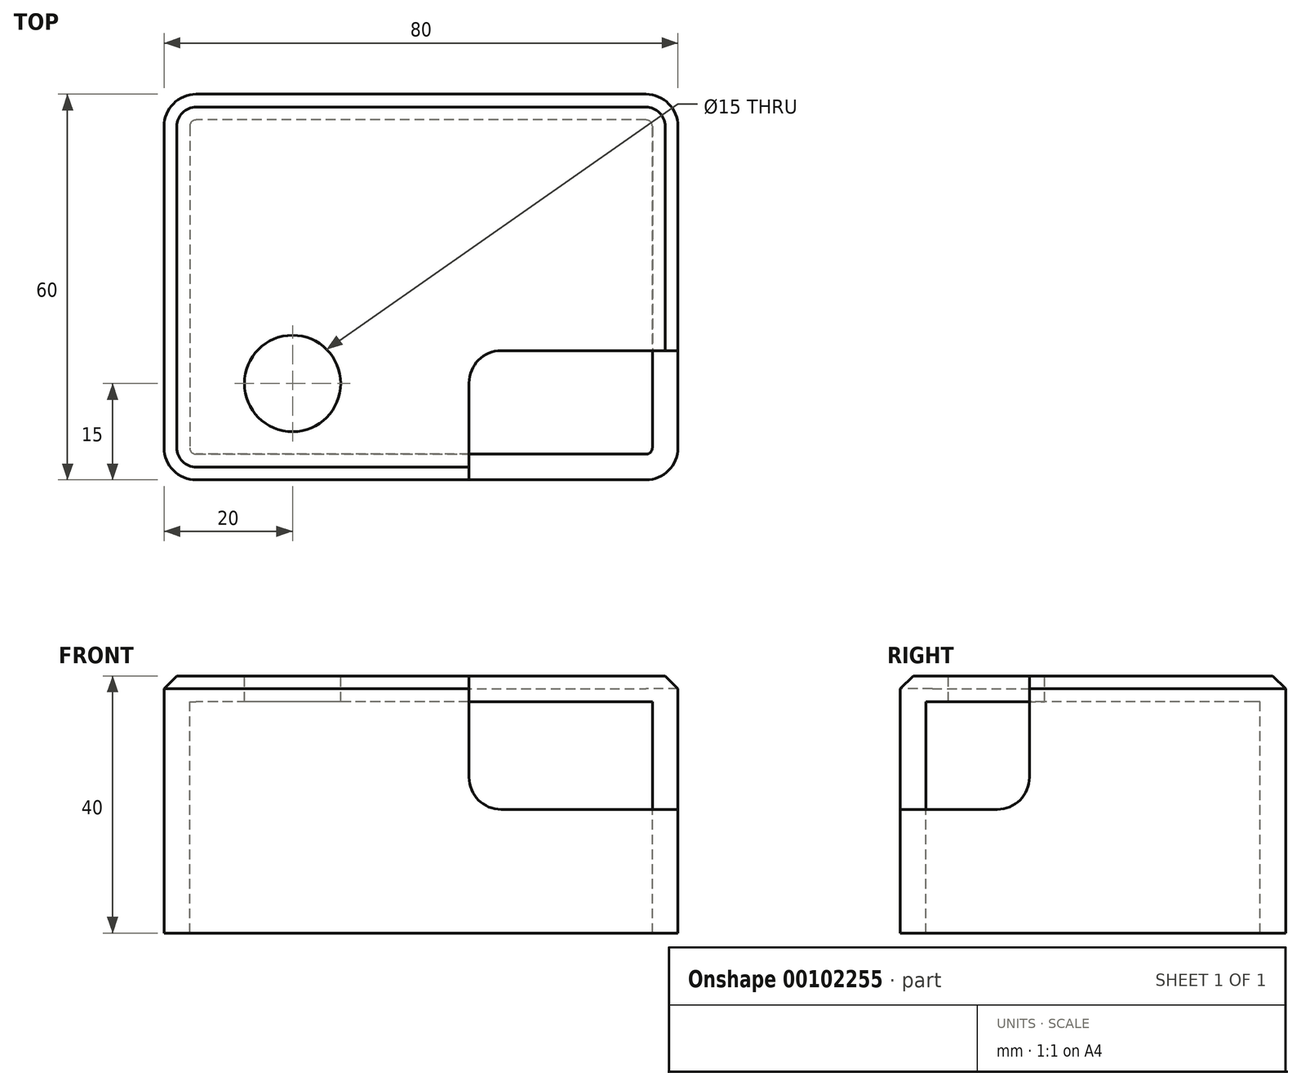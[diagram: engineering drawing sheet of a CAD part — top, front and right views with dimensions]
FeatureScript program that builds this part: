
annotation { "Feature Type Name" : "Feature", "Feature Type Description" : "" }
export const myFeature = defineFeature(function(context is Context, id is Id, definition is map)
    precondition{}
    {
        {
            var Q0;
            Q0=qCreatedBy(makeId("Top.planeOp"),FACE);
            var sketch = newSketch(context, id + "F0", { "sketchPlane" : qUnion([Q0])});
            skLineSegment(sketch, "E0.bottom", {"start": v(0, 0) * mm, "end": v(80, 0) * mm});
            skLineSegment(sketch, "E0.top", {"start": v(0, 60) * mm, "end": v(80, 60) * mm});
            skLineSegment(sketch, "E0.left", {"start": v(0, 0) * mm, "end": v(0, 60) * mm});
            skLineSegment(sketch, "E0.right", {"start": v(80, 0) * mm, "end": v(80, 60) * mm});
            skSolve(sketch);
        }
        {
            var Q0;
            Q0=makeQuery(id+"F0.imprint","IMPRINT",FACE,{"disambiguationData":[TD([[makeQuery(id+"F0.imprint","IMPRINT",EDGE,{"derivedFrom":sQuery(id+"F0.wireOp",EDGE,"E0.bottom")}),1.0]])]});
            extrude(context, id + "F1", {"entities" : qUnion([Q0]), "depth" : 40 * mm});
        }
        {
            var Q0;
            Q0=makeQuery(id+"F1.opExtrude","SWEPT_EDGE",EDGE,{"disambiguationData":[OSD([sQuery(id+"F0.wireOp",EDGE,"E0.top"),sQuery(id+"F0.wireOp",EDGE,"E0.right")])]});
            var Q1;
            Q1=makeQuery(id+"F1.opExtrude","SWEPT_EDGE",EDGE,{"disambiguationData":[OSD([sQuery(id+"F0.wireOp",EDGE,"E0.bottom"),sQuery(id+"F0.wireOp",EDGE,"E0.right")])]});
            var Q2;
            Q2=makeQuery(id+"F1.opExtrude","SWEPT_EDGE",EDGE,{"disambiguationData":[OSD([sQuery(id+"F0.wireOp",EDGE,"E0.bottom"),sQuery(id+"F0.wireOp",EDGE,"E0.left")])]});
            var Q3;
            Q3=makeQuery(id+"F1.opExtrude","SWEPT_EDGE",EDGE,{"disambiguationData":[OSD([sQuery(id+"F0.wireOp",EDGE,"E0.top"),sQuery(id+"F0.wireOp",EDGE,"E0.left")])]});
            fillet(context, id + "F2", {"entities" : qUnion([Q0, Q1, Q2, Q3]), "radius" : 5 * mm, "tangentPropagation" : true, "allowEdgeOverflow" : false});
        }
        {
            var Q0;
            Q0=makeQuery(id+"F1.opExtrude","CAP_EDGE",EDGE,{"disambiguationData":[OSD([sQuery(id+"F0.wireOp",EDGE,"E0.bottom")])],"isStart":false});
            chamfer(context, id + "F3", {"entities" : qUnion([Q0]), "width" : 2 * mm, "tangentPropagation" : true});
        }
        {
            var Q0;
            Q0=makeQuery(id+"F1.opExtrude","CAP_FACE",FACE,{"disambiguationData":[OSD([sQuery(id+"F0.wireOp",EDGE,"E0.bottom"),sQuery(id+"F0.wireOp",EDGE,"E0.top"),sQuery(id+"F0.wireOp",EDGE,"E0.left"),sQuery(id+"F0.wireOp",EDGE,"E0.right")])],"isStart":true});
            shell(context, id + "F4", {"entities" : qUnion([Q0]), "thickness" : 4 * mm});
        }
        {
            var Q0;
            Q0=makeQuery(id+"F1.opExtrude","CAP_FACE",FACE,{"disambiguationData":[OSD([sQuery(id+"F0.wireOp",EDGE,"E0.bottom"),sQuery(id+"F0.wireOp",EDGE,"E0.top"),sQuery(id+"F0.wireOp",EDGE,"E0.left"),sQuery(id+"F0.wireOp",EDGE,"E0.right")])],"isStart":false});
            var sketch = newSketch(context, id + "F5", { "sketchPlane" : qUnion([Q0])});
            skCircle(sketch, "E1", {"center": v(20, 15) * mm, "radius": 7.5 * mm});
            skSolve(sketch);
        }
        {
            var Q0;
            Q0 = qSketchRegion(id + "F5", true);
            extrude(context, id + "F6", {"entities" : qUnion([Q0]), "operationType" : NewBodyOperationType.REMOVE, "endBound" : BoundingType.THROUGH_ALL, "oppositeDirection" : true, "depth" : 25 * mm});
        }
        {
            var Q0;
            Q0=makeQuery(id+"F1.opExtrude","SWEPT_FACE",FACE,{"disambiguationData":[OSD([sQuery(id+"F0.wireOp",EDGE,"E0.bottom")])]});
            var sketch = newSketch(context, id + "F7", { "sketchPlane" : qUnion([Q0])});
            skLineSegment(sketch, "E2.bottom", {"start": v(47.48, 19.23) * mm, "end": v(94.75, 19.23) * mm});
            skLineSegment(sketch, "E2.top", {"start": v(47.48, 48.47) * mm, "end": v(94.75, 48.47) * mm});
            skLineSegment(sketch, "E2.left", {"start": v(47.48, 19.23) * mm, "end": v(47.48, 48.47) * mm});
            skLineSegment(sketch, "E2.right", {"start": v(94.75, 19.23) * mm, "end": v(94.75, 48.47) * mm});
            skSolve(sketch);
        }
        {
            var Q0;
            Q0 = qSketchRegion(id + "F7", true);
            extrude(context, id + "F8", {"entities" : qUnion([Q0]), "operationType" : NewBodyOperationType.REMOVE, "oppositeDirection" : true, "depth" : 20.1 * mm});
        }
        {
            var Q0;
            Q0=makeQuery(id+"F8.boolean.opBoolean","COPY",EDGE,{"derivedFrom":makeQuery(id+"F8.opExtrude","SWEPT_EDGE",EDGE,{"disambiguationData":[OSD([sQuery(id+"F7.wireOp",EDGE,"E2.bottom"),sQuery(id+"F7.wireOp",EDGE,"E2.left")])]})});
            var Q1;
            Q1=makeQuery(id+"F8.boolean.opBoolean","COPY",EDGE,{"derivedFrom":makeQuery(id+"F8.opExtrude","CAP_EDGE",EDGE,{"disambiguationData":[OSD([sQuery(id+"F7.wireOp",EDGE,"E2.left")])],"isStart":false})});
            var Q2;
            Q2=makeQuery(id+"F8.boolean.opBoolean","COPY",EDGE,{"derivedFrom":makeQuery(id+"F8.opExtrude","CAP_EDGE",EDGE,{"disambiguationData":[OSD([sQuery(id+"F7.wireOp",EDGE,"E2.bottom")])],"isStart":false})});
            fillet(context, id + "F9", {"entities" : qUnion([Q0, Q1, Q2]), "radius" : 5 * mm, "tangentPropagation" : true, "allowEdgeOverflow" : false});
        }
    });
